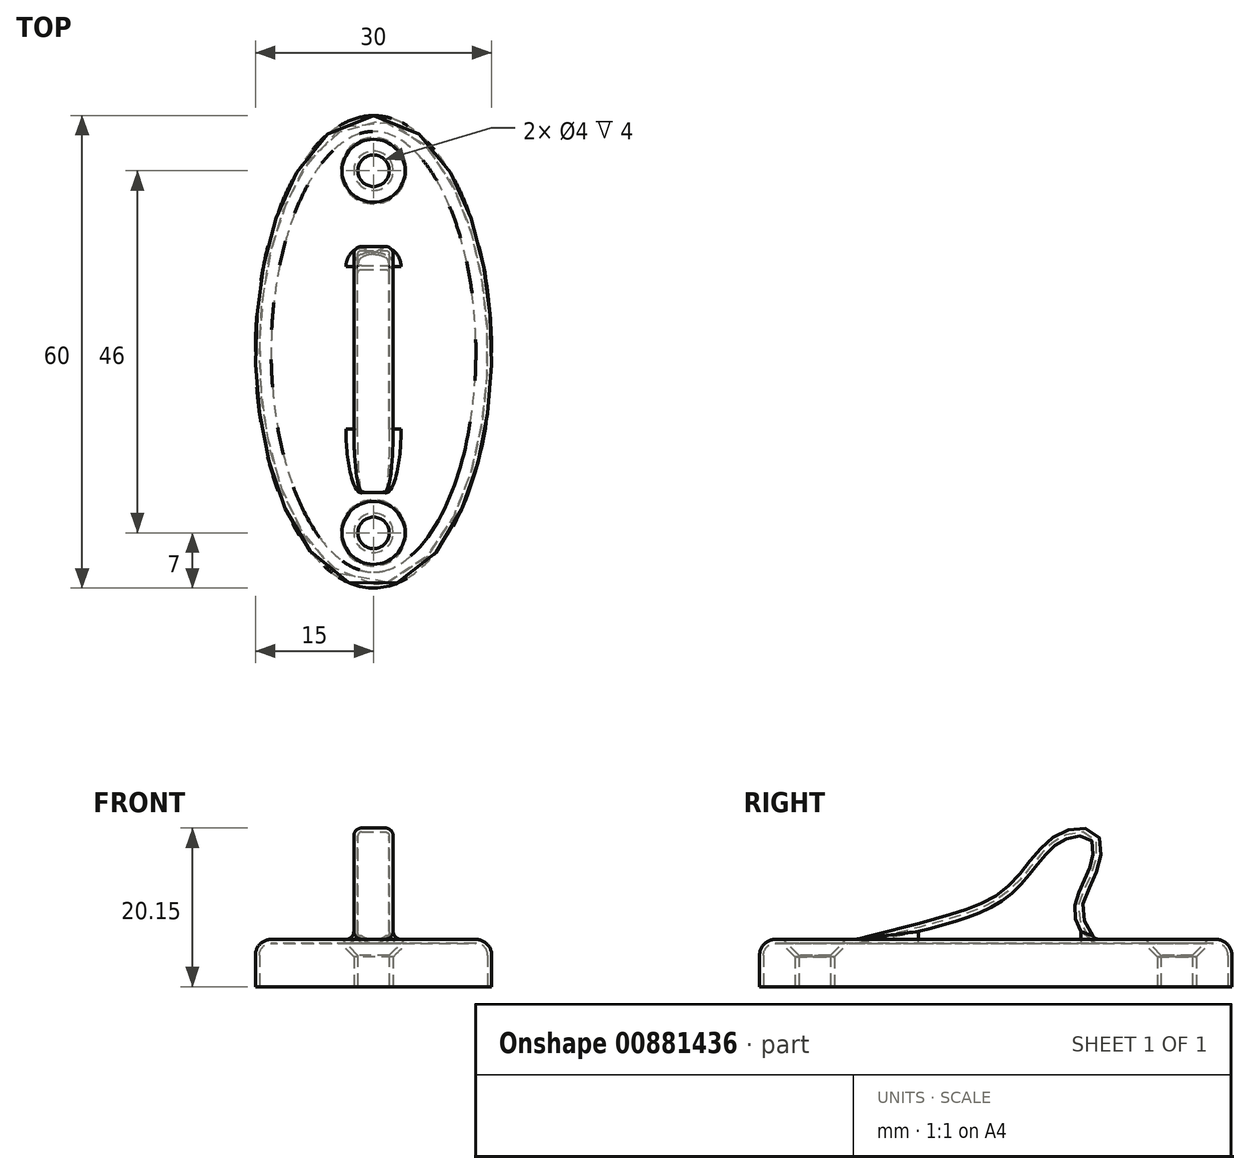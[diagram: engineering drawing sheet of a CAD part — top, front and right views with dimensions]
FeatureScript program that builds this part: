
annotation { "Feature Type Name" : "Feature", "Feature Type Description" : "" }
export const myFeature = defineFeature(function(context is Context, id is Id, definition is map)
    precondition{}
    {
        {
            var Q0;
            Q0=qCreatedBy(makeId("Top.planeOp"),FACE);
            var sketch = newSketch(context, id + "F0", { "sketchPlane" : qUnion([Q0])});
            skEllipse(sketch, "E0", {"center": v(0, 0) * mm, "majorRadius": 30 * mm, "minorRadius": 15 * mm, "majorAxis": v(0, 1)});
            skLineSegment(sketch, "E1", {"start": v(0, 0) * mm, "end": v(0, 30) * mm, "construction": true});
            skCircle(sketch, "E2", {"center": v(0, 23) * mm, "radius": 2 * mm});
            skLineSegment(sketch, "E3", {"start": v(0, 0) * mm, "end": v(-15, 0) * mm, "construction": true});
            skCircle(sketch, "E4.MirrorC", {"center": v(0, -23) * mm, "radius": 2 * mm});
            skSolve(sketch);
        }
        {
            var Q0;
            Q0 = qSketchRegion(id + "F0", true);
            extrude(context, id + "F1", {"entities" : qUnion([Q0]), "depth" : 6 * mm, "offsetDistance" : 25 * mm});
        }
        {
            var Q0;
            Q0=qCreatedBy(makeId("Right.planeOp"),FACE);
            var sketch = newSketch(context, id + "F2", { "sketchPlane" : qUnion([Q0])});
            skLineSegment(sketch, "E5.0", {"start": v(-17.84, 6) * mm, "end": v(12.65, 6) * mm});
            skFitSpline(sketch, "E6", {"points": [v(-17.84, 6) * mm, v(-6.79, 8.86) * mm, v(0, 11.55) * mm, v(3.94, 15.4) * mm, v(8.3, 19.59) * mm, v(12.65, 19.59) * mm, v(13.32, 16.57) * mm, v(12.15, 13.05) * mm, v(10.97, 9.53) * mm, v(12.65, 6) * mm], "startDerivative": vector(70.51, 17.48) * mm, "endDerivative": vector(25.3, -36.44) * mm});
            skPoint(sketch, "E7.orphan", {"position": v(-30, 6) * mm});
            skPoint(sketch, "E8.orphan", {"position": v(30, 6) * mm});
            skSolve(sketch);
        }
        {
            var Q0;
            Q0 = qSketchRegion(id + "F2", true);
            extrude(context, id + "F3", {"entities" : qUnion([Q0]), "operationType" : NewBodyOperationType.ADD, "endBound" : BoundingType.SYMMETRIC, "depth" : 5 * mm, "offsetDistance" : 25 * mm});
        }
        {
            var Q0;
            Q0=makeQuery(id+"F1.opExtrude","CAP_EDGE",EDGE,{"disambiguationData":[OSD([sQuery(id+"F0.wireOp",EDGE,"E2")])],"isStart":false});
            var Q1;
            Q1=makeQuery(id+"F1.opExtrude","CAP_EDGE",EDGE,{"disambiguationData":[OSD([sQuery(id+"F0.wireOp",EDGE,"E4.MirrorC")])],"isStart":false});
            chamfer(context, id + "F4", {"entities" : qUnion([Q0, Q1]), "width" : 2 * mm, "tangentPropagation" : true});
        }
        {
            var Q0;
            Q0=makeQuery(id+"F1.opExtrude","CAP_EDGE",EDGE,{"disambiguationData":[OSD([sQuery(id+"F0.wireOp",EDGE,"E0")])],"isStart":false});
            fillet(context, id + "F5", {"entities" : qUnion([Q0]), "radius" : 2 * mm, "tangentPropagation" : true, "allowEdgeOverflow" : false});
        }
        {
            var Q0;
            Q0=makeQuery(id+"F3.opExtrude","CAP_FACE",FACE,{"disambiguationData":[OSD([sQuery(id+"F2.wireOp",EDGE,"E5.0"),sQuery(id+"F2.wireOp",EDGE,"E6")])],"isStart":false});
            var Q1;
            {var subQ0=sQuery(id+"F2.wireOp",EDGE,"E6");var subQ1=sQuery(id+"F2.wireOp",EDGE,"E5.0");Q1=makeQuery(id+"F3.opExtrude","SWEPT_EDGE",EDGE,{"disambiguationData":[OSD([subQ1,subQ0]),TDD([makeQuery(id+"F2.imprint","INTERSECT",VERTEX,{"disambiguationData":[OD(1.0)],"derivedFrom":[subQ1,subQ0]})])]});}
            var Q2;
            Q2=makeQuery(id+"F3.opExtrude","CAP_FACE",FACE,{"disambiguationData":[OSD([sQuery(id+"F2.wireOp",EDGE,"E5.0"),sQuery(id+"F2.wireOp",EDGE,"E6")])],"isStart":true});
            fillet(context, id + "F6", {"entities" : qUnion([Q0, Q1, Q2]), "radius" : 1 * mm, "tangentPropagation" : true, "allowEdgeOverflow" : false});
        }
        {
            var Q0;
            Q0=makeQuery(id+"F1.opExtrude","CAP_FACE",FACE,{"disambiguationData":[OSD([sQuery(id+"F0.wireOp",EDGE,"E0"),sQuery(id+"F0.wireOp",EDGE,"E2")])],"isStart":true});
            shell(context, id + "F7", {"entities" : qUnion([Q0]), "thickness" : 0.5 * mm});
        }
    });
